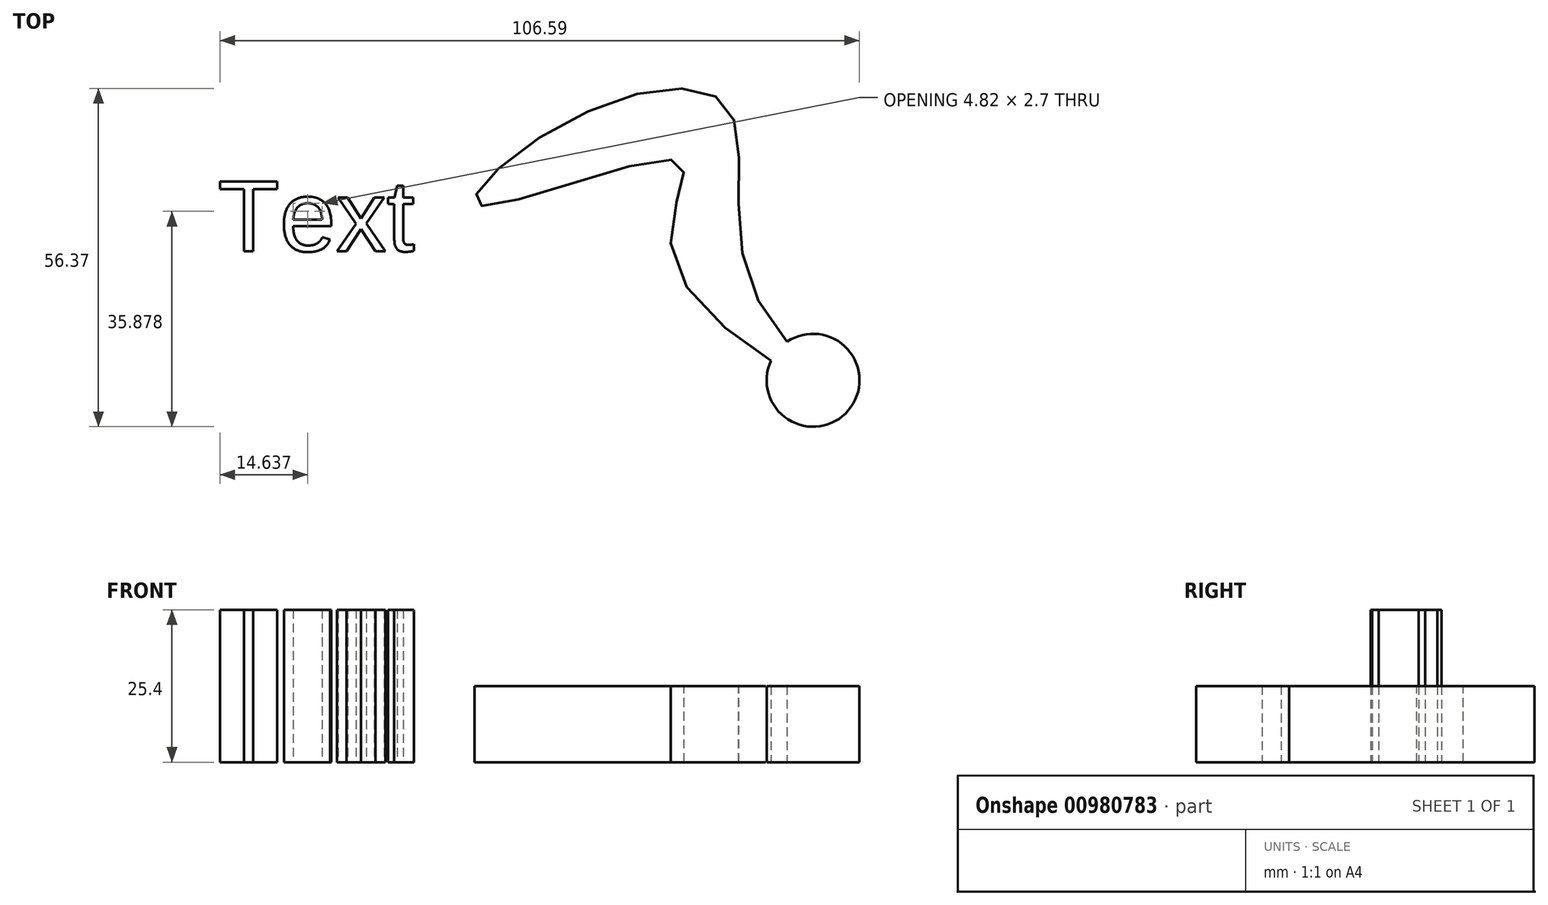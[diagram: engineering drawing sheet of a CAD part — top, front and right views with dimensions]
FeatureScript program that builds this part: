
annotation { "Feature Type Name" : "Feature", "Feature Type Description" : "" }
export const myFeature = defineFeature(function(context is Context, id is Id, definition is map)
    precondition{}
    {
        {
            var Q0;
            Q0=qCreatedBy(makeId("Top.planeOp"),FACE);
            var sketch = newSketch(context, id + "F0", { "sketchPlane" : qUnion([Q0])});
            skFitSpline(sketch, "E0", {"points": [v(-21.85, 33.28) * mm, v(11.34, 40.65) * mm, v(10.6, 24.06) * mm, v(35.3, 3.41) * mm, v(23.5, 20) * mm, v(19.45, 49.87) * mm, v(-7.84, 46.92) * mm, v(-21.85, 33.28) * mm]});
            skSolve(sketch);
        }
        {
            var Q0;
            Q0 = qSketchRegion(id + "F0", true);
            extrude(context, id + "F1", {"entities" : qUnion([Q0]), "depth" : 12.7 * mm, "offsetDistance" : 25.4 * mm});
        }
        {
            var Q0;
            Q0=qCreatedBy(makeId("Top.planeOp"),FACE);
            var sketch = newSketch(context, id + "F2", { "sketchPlane" : qUnion([Q0])});
            skCircle(sketch, "E1", {"center": v(33.83, 4.15) * mm, "radius": 7.74 * mm});
            skSolve(sketch);
        }
        {
            var Q0;
            Q0=makeQuery(id+"F2.imprint","IMPRINT",FACE,{"disambiguationData":[TD([[makeQuery(id+"F2.imprint","IMPRINT",EDGE,{"derivedFrom":sQuery(id+"F2.wireOp",EDGE,"E1")}),1.0]])]});
            var Q1;
            Q1=sQuery(id+"F2.wireOp",EDGE,"E1");
            var Q2;
            Q2=makeQuery(id+"F1.opExtrude","CAP_FACE",FACE,{"disambiguationData":[OSD([sQuery(id+"F0.wireOp",EDGE,"E0")])],"isStart":false});
            extrude(context, id + "F3", {"entities" : qUnion([Q0]), "operationType" : NewBodyOperationType.ADD, "surfaceOperationType" : NewSurfaceOperationType.ADD, "surfaceEntities" : qUnion([Q1]), "endBound" : BoundingType.UP_TO_SURFACE, "depth" : 25.4 * mm, "endBoundEntityFace" : qUnion([Q2]), "offsetDistance" : 25.4 * mm});
        }
        {
            var Q0;
            Q0=qCreatedBy(makeId("Top.planeOp"),FACE);
            var sketch = newSketch(context, id + "F4", { "sketchPlane" : qUnion([Q0])});
            skText(sketch, "E2", { "text": "Text", "fontName": "Arimo-Regular.ttf"});
            const initialGuessF4  = {"E2": [-0.0654, 0.02565, 1, 0, 0.01216]};
            skSetInitialGuess(sketch, initialGuessF4);
            skSolve(sketch);
        }
        {
            var Q0;
            Q0 = qSketchRegion(id + "F4", true);
            extrude(context, id + "F5", {"entities" : qUnion([Q0]), "depth" : 25.4 * mm, "offsetDistance" : 25.4 * mm});
        }
    });
